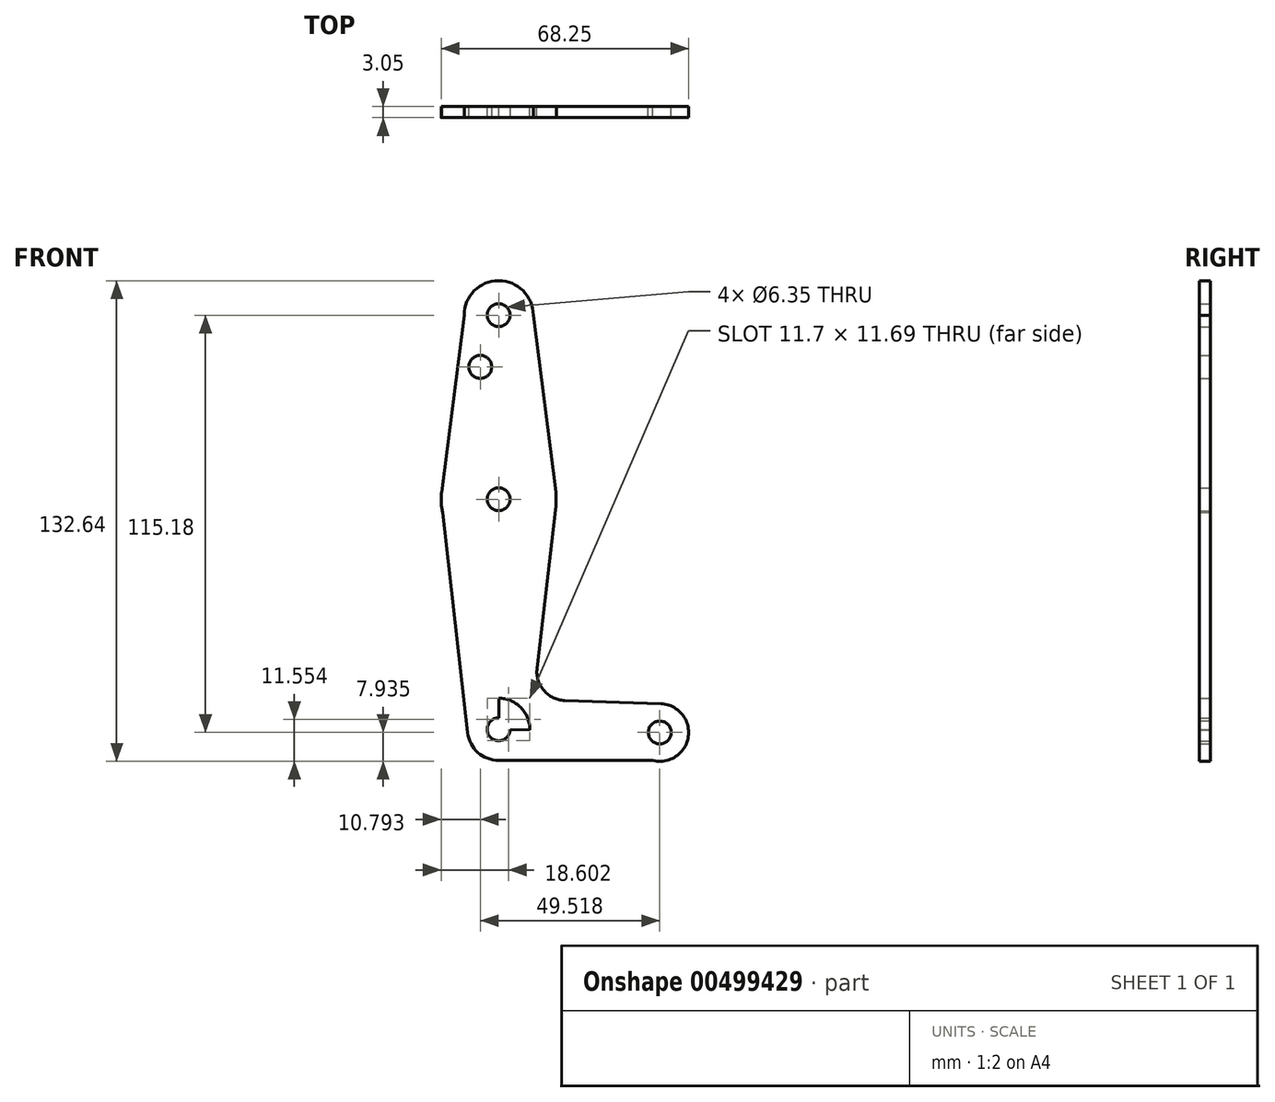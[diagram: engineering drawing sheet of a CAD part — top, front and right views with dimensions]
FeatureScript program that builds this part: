
annotation { "Feature Type Name" : "Feature", "Feature Type Description" : "" }
export const myFeature = defineFeature(function(context is Context, id is Id, definition is map)
    precondition{}
    {
        {
            var Q0;
            Q0=qCreatedBy(makeId("Front.planeOp"),FACE);
            var sketch = newSketch(context, id + "F0", { "sketchPlane" : qUnion([Q0])});
            skCircle(sketch, "E0", {"center": v(0, 64.98) * mm, "radius": 9.53 * mm});
            skCircle(sketch, "E1", {"center": v(0, 14.18) * mm, "radius": 15.88 * mm});
            skCircle(sketch, "E2", {"center": v(0, -49.32) * mm, "radius": 8.58 * mm});
            skCircle(sketch, "E3", {"center": v(44.44, -50.2) * mm, "radius": 7.94 * mm});
            skLineSegment(sketch, "E4", {"start": v(0, 64.98) * mm, "end": v(0, -49.32) * mm});
            skLineSegment(sketch, "E5", {"start": v(44.44, -50.2) * mm, "end": v(0, -49.32) * mm});
            skLineSegment(sketch, "E6", {"start": v(9.53, 64.98) * mm, "end": v(15.75, 16.18) * mm});
            skLineSegment(sketch, "E7", {"start": v(-9.53, 64.98) * mm, "end": v(-15.75, 16.18) * mm});
            skLineSegment(sketch, "E8", {"start": v(15.78, 12.4) * mm, "end": v(10.59, -32.5) * mm});
            skLineSegment(sketch, "E9", {"start": v(-15.88, 14.18) * mm, "end": v(-8.53, -50.3) * mm});
            skLineSegment(sketch, "E10", {"start": v(18.21, -41.36) * mm, "end": v(44.71, -42.27) * mm});
            skLineSegment(sketch, "E11", {"start": v(0, -57.9) * mm, "end": v(42.53, -57.9) * mm});
            skCircle(sketch, "E12", {"center": v(0, 64.98) * mm, "radius": 3.18 * mm});
            skCircle(sketch, "E13", {"center": v(-5.08, 50.7) * mm, "radius": 3.18 * mm});
            skCircle(sketch, "E14", {"center": v(0, 14.18) * mm, "radius": 3.18 * mm});
            skCircle(sketch, "E15", {"center": v(0, -49.32) * mm, "radius": 3.18 * mm});
            skCircle(sketch, "E16", {"center": v(44.44, -50.2) * mm, "radius": 3.18 * mm});
            skArc(sketch, "E17.filletArc", {"start": v(10.59, -32.5) * mm, "mid": v(12.46, -38.6) * mm, "end": v(18.21, -41.36) * mm});
            skSolve(sketch);
        }
        {
            var Q0;
            Q0 = qSketchRegion(id + "F0", true);
            extrude(context, id + "F1", {"entities" : qUnion([Q0]), "depth" : 3.05 * mm});
        }
    });
